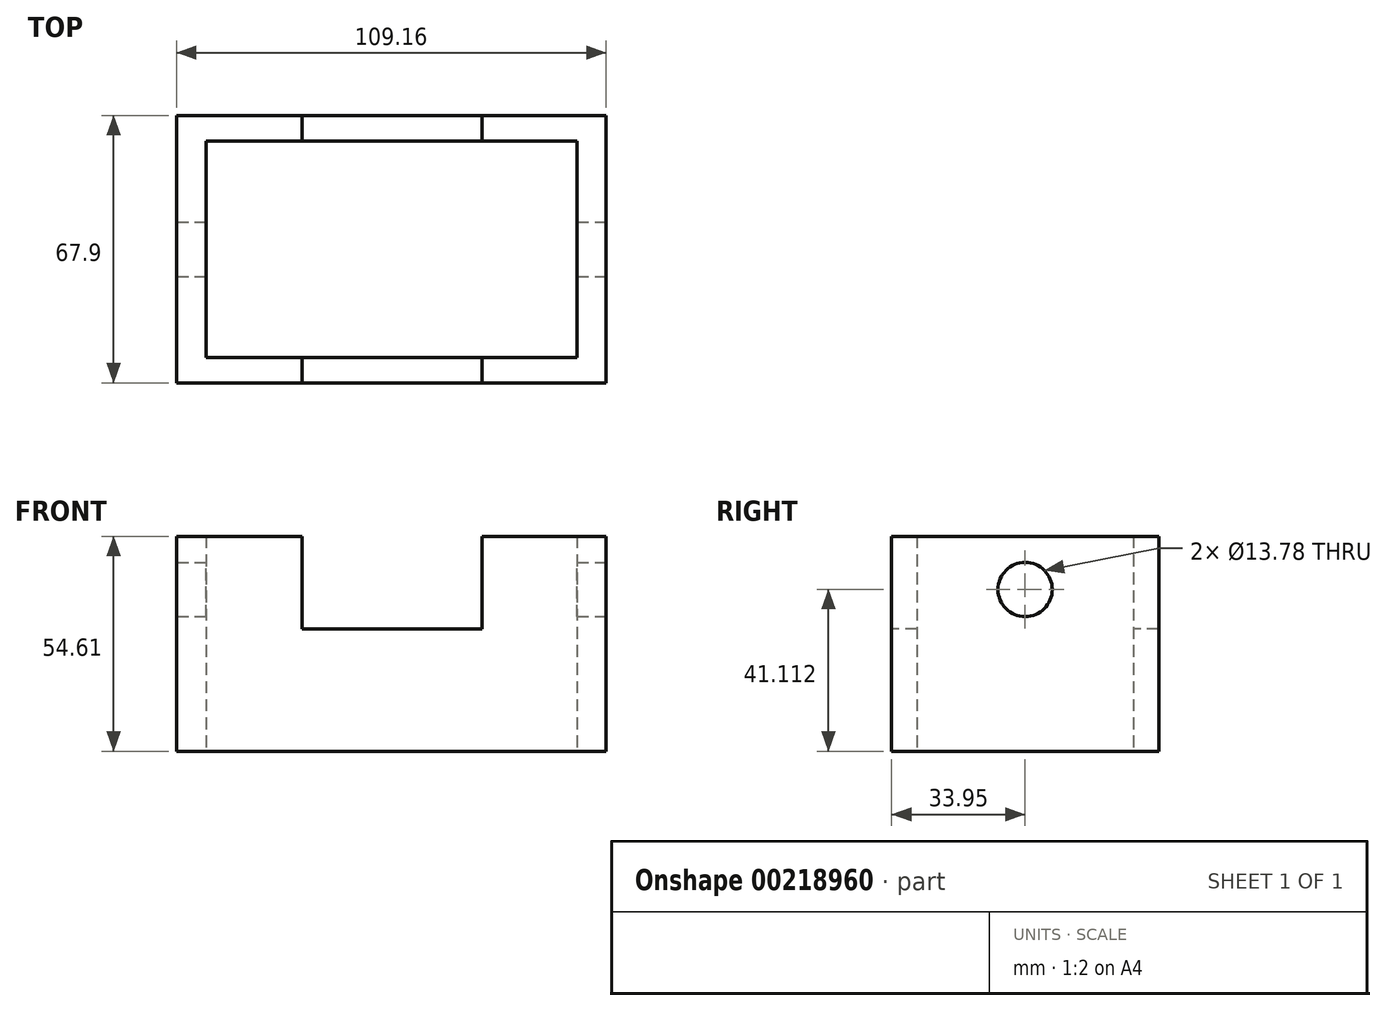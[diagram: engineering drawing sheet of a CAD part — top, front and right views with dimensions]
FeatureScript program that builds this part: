
annotation { "Feature Type Name" : "Feature", "Feature Type Description" : "" }
export const myFeature = defineFeature(function(context is Context, id is Id, definition is map)
    precondition{}
    {
        {
            var Q0;
            Q0=qCreatedBy(makeId("Top.planeOp"),FACE);
            var sketch = newSketch(context, id + "F0", { "sketchPlane" : qUnion([Q0])});
            skLineSegment(sketch, "E0.bottom", {"start": v(54.58, 33.95) * mm, "end": v(-54.58, 33.95) * mm});
            skLineSegment(sketch, "E0.top", {"start": v(54.58, -33.95) * mm, "end": v(-54.58, -33.95) * mm});
            skLineSegment(sketch, "E0.left", {"start": v(54.58, 33.95) * mm, "end": v(54.58, -33.95) * mm});
            skLineSegment(sketch, "E0.right", {"start": v(-54.58, 33.95) * mm, "end": v(-54.58, -33.95) * mm});
            skPoint(sketch, "E0.middle", {"position": v(0, 0) * mm});
            skLineSegment(sketch, "E1.bottom", {"start": v(47.1, 27.45) * mm, "end": v(-47.1, 27.45) * mm});
            skLineSegment(sketch, "E1.top", {"start": v(47.1, -27.45) * mm, "end": v(-47.1, -27.45) * mm});
            skLineSegment(sketch, "E1.left", {"start": v(47.1, 27.45) * mm, "end": v(47.1, -27.45) * mm});
            skLineSegment(sketch, "E1.right", {"start": v(-47.1, 27.45) * mm, "end": v(-47.1, -27.45) * mm});
            skSolve(sketch);
        }
        {
            var Q0;
            Q0=makeQuery(id+"F0.imprint","IMPRINT",FACE,{"disambiguationData":[TD([[makeQuery(id+"F0.imprint","IMPRINT",EDGE,{"derivedFrom":sQuery(id+"F0.wireOp",EDGE,"E0.bottom")}),1.0]])]});
            extrude(context, id + "F1", {"entities" : qUnion([Q0]), "depth" : 54.6 * mm});
        }
        {
            var Q0;
            Q0=makeQuery(id+"F1.opExtrude","SWEPT_FACE",FACE,{"disambiguationData":[OSD([sQuery(id+"F0.wireOp",EDGE,"E0.top")])]});
            var sketch = newSketch(context, id + "F2", { "sketchPlane" : qUnion([Q0])});
            skLineSegment(sketch, "E2.top", {"start": v(-22.74, 31.04) * mm, "end": v(23.07, 31.04) * mm});
            skLineSegment(sketch, "E2.left", {"start": v(-22.74, 54.61) * mm, "end": v(-22.74, 31.04) * mm});
            skLineSegment(sketch, "E2.right", {"start": v(23.07, 54.61) * mm, "end": v(23.07, 31.04) * mm});
            skSolve(sketch);
        }
        {
            var Q0;
            Q0=makeQuery(id+"F2.imprint","IMPRINT",FACE,{"disambiguationData":[TD([[makeQuery(id+"F2.imprint","IMPRINT",EDGE,{"derivedFrom":sQuery(id+"F2.wireOp",EDGE,"E2.top")}),1.0]])]});
            extrude(context, id + "F3", {"entities" : qUnion([Q0]), "operationType" : NewBodyOperationType.REMOVE, "endBound" : BoundingType.THROUGH_ALL, "oppositeDirection" : true, "depth" : 25.4 * mm});
        }
        {
            var Q0;
            Q0=makeQuery(id+"F1.opExtrude","SWEPT_FACE",FACE,{"disambiguationData":[OSD([sQuery(id+"F0.wireOp",EDGE,"E0.left")])]});
            var sketch = newSketch(context, id + "F4", { "sketchPlane" : qUnion([Q0])});
            skCircle(sketch, "E3", {"center": v(0, 41.11) * mm, "radius": 6.9 * mm});
            skSolve(sketch);
        }
        {
            var Q0;
            Q0=makeQuery(id+"F4.imprint","IMPRINT",FACE,{"disambiguationData":[TD([[makeQuery(id+"F4.imprint","IMPRINT",EDGE,{"derivedFrom":sQuery(id+"F4.wireOp",EDGE,"E3")}),1.0]])]});
            extrude(context, id + "F5", {"entities" : qUnion([Q0]), "operationType" : NewBodyOperationType.REMOVE, "endBound" : BoundingType.THROUGH_ALL, "oppositeDirection" : true, "depth" : 25.4 * mm});
        }
    });
